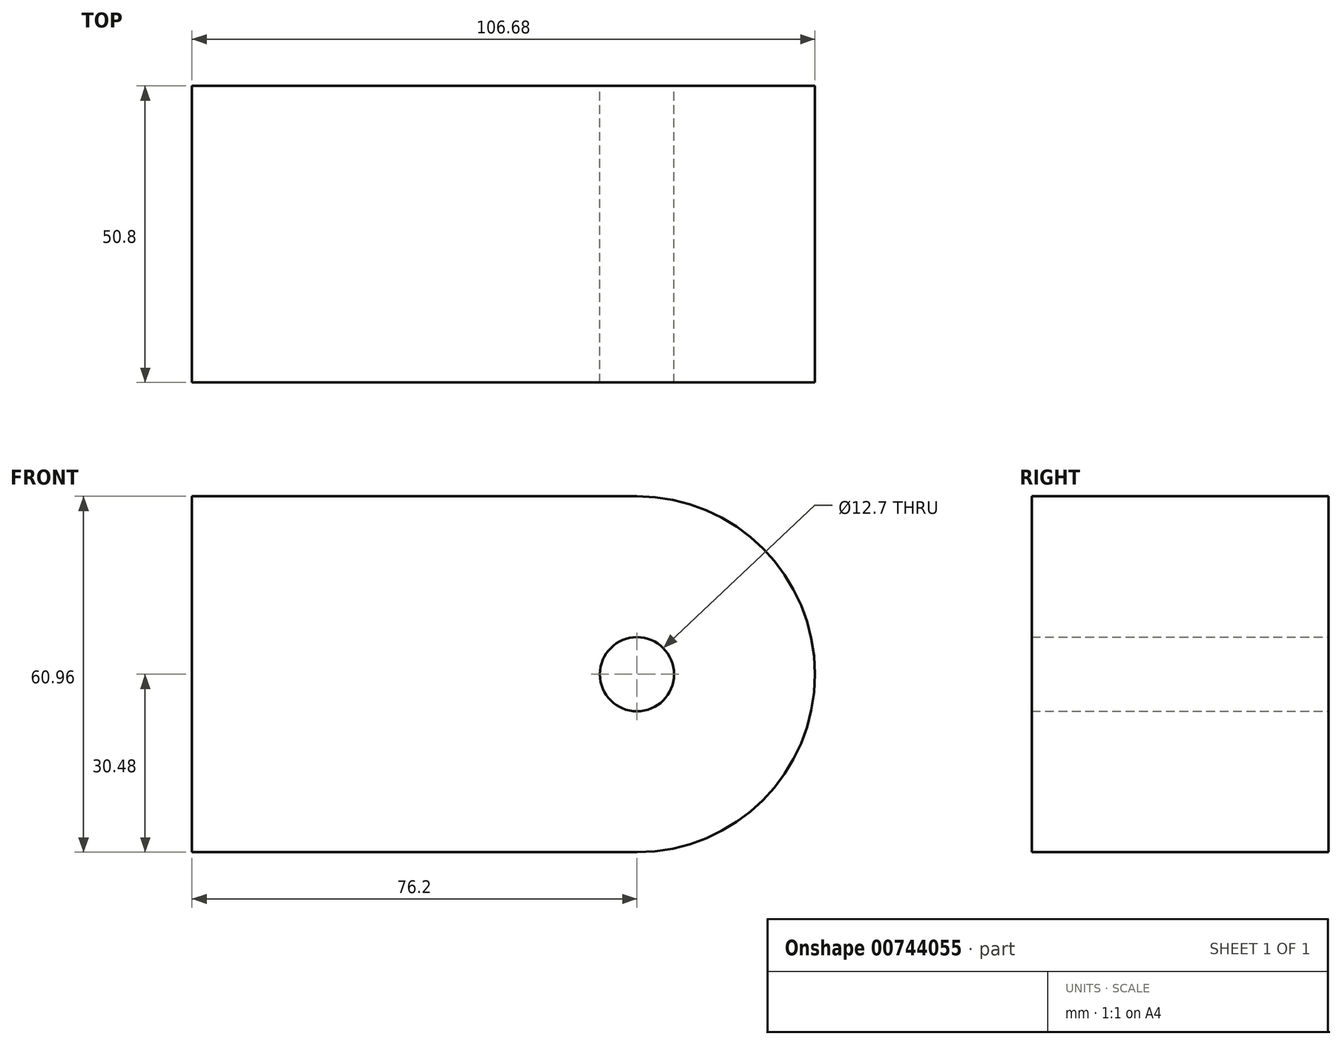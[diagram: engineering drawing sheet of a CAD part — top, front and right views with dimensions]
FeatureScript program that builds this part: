
annotation { "Feature Type Name" : "Feature", "Feature Type Description" : "" }
export const myFeature = defineFeature(function(context is Context, id is Id, definition is map)
    precondition{}
    {
        {
            var Q0;
            Q0=qCreatedBy(makeId("Front.planeOp"),FACE);
            var sketch = newSketch(context, id + "F0", { "sketchPlane" : qUnion([Q0])});
            skLineSegment(sketch, "E0.bottom", {"start": v(0, 0) * mm, "end": v(76.2, 0) * mm});
            skLineSegment(sketch, "E0.top", {"start": v(0, 60.96) * mm, "end": v(76.2, 60.96) * mm});
            skLineSegment(sketch, "E0.left", {"start": v(0, 0) * mm, "end": v(0, 60.96) * mm});
            skArc(sketch, "E1", {"start": v(76.2, 0) * mm, "mid": v(106.68, 30.48) * mm, "end": v(76.2, 60.96) * mm});
            skCircle(sketch, "E2", {"center": v(76.2, 30.48) * mm, "radius": 6.35 * mm});
            skSolve(sketch);
        }
        {
            var Q0;
            Q0=makeQuery(id+"F0.imprint","IMPRINT",FACE,{"disambiguationData":[TD([[makeQuery(id+"F0.imprint","IMPRINT",EDGE,{"derivedFrom":sQuery(id+"F0.wireOp",EDGE,"E0.bottom")}),1.0]])]});
            extrude(context, id + "F1", {"entities" : qUnion([Q0]), "depth" : 50.8 * mm, "offsetDistance" : 25.4 * mm});
        }
    });
